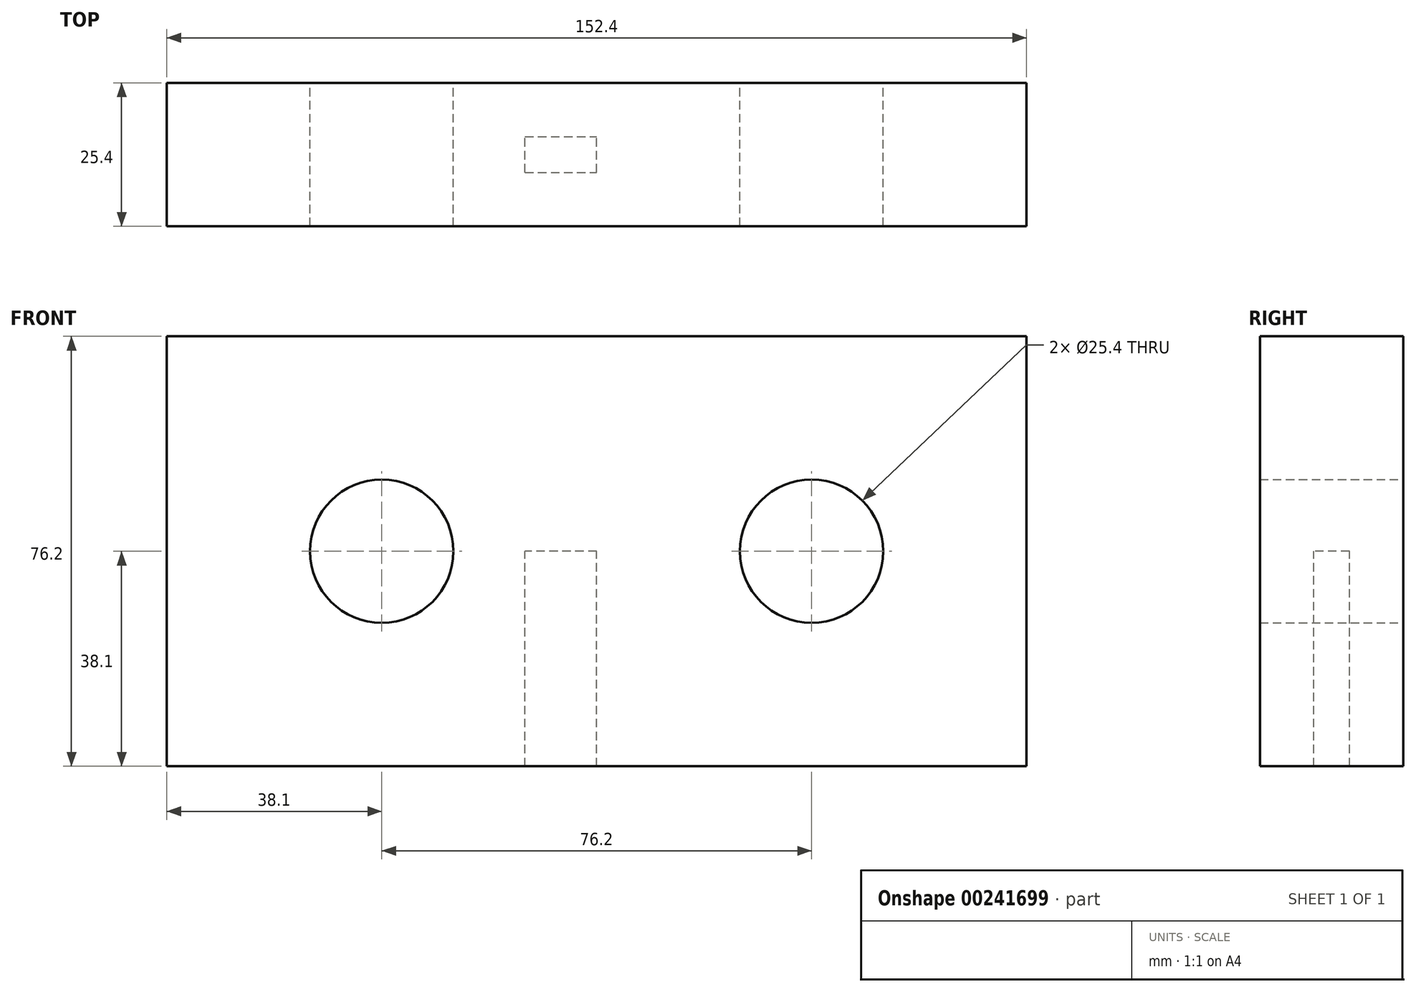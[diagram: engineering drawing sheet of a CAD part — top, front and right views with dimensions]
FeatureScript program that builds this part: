
annotation { "Feature Type Name" : "Feature", "Feature Type Description" : "" }
export const myFeature = defineFeature(function(context is Context, id is Id, definition is map)
    precondition{}
    {
        {
            var Q0;
            Q0=qCreatedBy(makeId("Front.planeOp"),FACE);
            var sketch = newSketch(context, id + "F0", { "sketchPlane" : qUnion([Q0])});
            skLineSegment(sketch, "E0.bottom", {"start": v(76.2, 38.1) * mm, "end": v(-76.2, 38.1) * mm});
            skLineSegment(sketch, "E0.top", {"start": v(76.2, -38.1) * mm, "end": v(-76.2, -38.1) * mm});
            skLineSegment(sketch, "E0.left", {"start": v(76.2, 38.1) * mm, "end": v(76.2, -38.1) * mm});
            skLineSegment(sketch, "E0.right", {"start": v(-76.2, 38.1) * mm, "end": v(-76.2, -38.1) * mm});
            skPoint(sketch, "E0.middle", {"position": v(0, 0) * mm});
            skLineSegment(sketch, "E1", {"start": v(0, 0) * mm, "end": v(-38.1, 0) * mm});
            skCircle(sketch, "E2", {"center": v(-38.1, 0) * mm, "radius": 12.7 * mm});
            skLineSegment(sketch, "E3", {"start": v(0, 0) * mm, "end": v(38.1, 0) * mm});
            skCircle(sketch, "E4", {"center": v(38.1, 0) * mm, "radius": 12.7 * mm});
            skSolve(sketch);
        }
        {
            var Q0;
            Q0=qCreatedBy(makeId("Top.planeOp"),FACE);
            var sketch = newSketch(context, id + "F1", { "sketchPlane" : qUnion([Q0])});
            skLineSegment(sketch, "E5", {"start": v(0, 0) * mm, "end": v(0, -9.53) * mm});
            skLineSegment(sketch, "E6.bottom", {"start": v(0, -9.53) * mm, "end": v(-12.7, -9.53) * mm});
            skLineSegment(sketch, "E6.top", {"start": v(0, -15.88) * mm, "end": v(-12.7, -15.88) * mm});
            skLineSegment(sketch, "E6.left", {"start": v(0, -9.53) * mm, "end": v(0, -15.88) * mm});
            skLineSegment(sketch, "E6.right", {"start": v(-12.7, -9.53) * mm, "end": v(-12.7, -15.88) * mm});
            skSolve(sketch);
        }
        {
            var Q0;
            Q0 = qSketchRegion(id + "F0", true);
            extrude(context, id + "F2", {"entities" : qUnion([Q0]), "depth" : 25.4 * mm});
        }
        {
            var Q0;
            Q0 = qSketchRegion(id + "F1", true);
            extrude(context, id + "F3", {"entities" : qUnion([Q0]), "operationType" : NewBodyOperationType.REMOVE, "oppositeDirection" : true, "depth" : 70.36 * mm});
        }
    });
